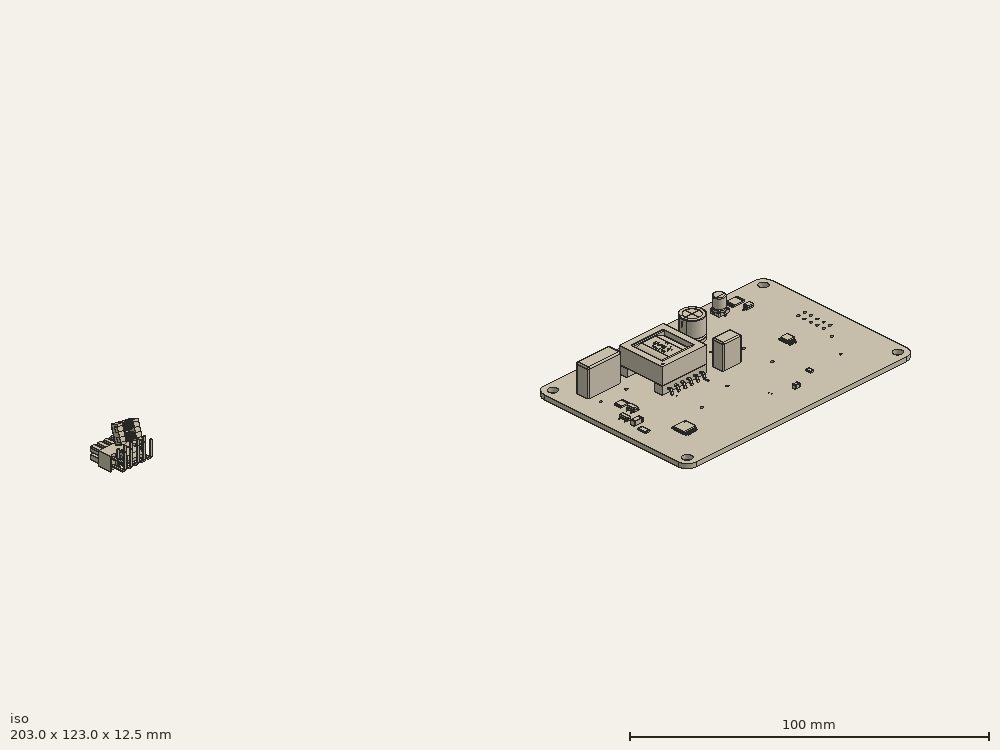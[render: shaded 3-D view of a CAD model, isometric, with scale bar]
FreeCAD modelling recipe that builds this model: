
FCSTD DOCUMENT  (FreeCAD 0.21R33694 (Git))
Label: nixiePSU
License: All rights reserved
LicenseURL: http://en.wikipedia.org/wiki/All_rights_reserved
objects: Part::Feature×79, App::Link×66, App::Part×19, PartDesign::CoordinateSystem×1, Sketcher::SketchObject×1
note: 81 computed .brp shape members not serialized (recipe doc carries the construction recipe); baked Part::Feature solids carry a one-line shape summary decoded from their .brp

FEATURE [PartDesign::CoordinateSystem] Local_CS_fa9e
  AttacherType = Attacher::AttachEngine3D
  MapMode = 2
  Support = -> [X_Axis001]
FEATURE [Part::Feature] Pcb_fa9e
  shape: bbox 90 x 60 x 1.6 mm, 44 faces (baked)
FEATURE [Sketcher::SketchObject] PCB_Sketch_fa9e
  FullyConstrained = false
  sketch-geometry (8):
    g0: LineSegment StartX=196.5 StartY=-58 StartZ=0 EndX=196.5 EndY=-111 EndZ=0
    g1: LineSegment StartX=110 StartY=-114.5 StartZ=0 EndX=193 EndY=-114.5 EndZ=0
    g2: LineSegment StartX=106.5 StartY=-58 StartZ=0 EndX=106.5 EndY=-111 EndZ=0
    g3: LineSegment StartX=110 StartY=-54.5 StartZ=0 EndX=193 EndY=-54.5 EndZ=0
    g4: ArcOfCircle CenterX=193 CenterY=-111 CenterZ=0 NormalX=0 NormalY=0 NormalZ=-1 AngleXU=3.14159 Radius=3.5 StartAngle=0 EndAngle=1.5708
    g5: ArcOfCircle CenterX=110 CenterY=-58 CenterZ=0 NormalX=0 NormalY=0 NormalZ=-1 AngleXU=-2.59331e-07 Radius=3.5 StartAngle=0 EndAngle=1.5708
    g6: ArcOfCircle CenterX=110 CenterY=-111 CenterZ=0 NormalX=0 NormalY=0 NormalZ=-1 AngleXU=-1.5708 Radius=3.5 StartAngle=0 EndAngle=1.5708
    g7: ArcOfCircle CenterX=193 CenterY=-58 CenterZ=0 NormalX=0 NormalY=0 NormalZ=-1 AngleXU=1.5708 Radius=3.5 StartAngle=0 EndAngle=1.5708
  constraints (8):
    c: Coincident(g2,g6)
    c: Coincident(g2,g5)
    c: Coincident(g1,g6)
    c: Coincident(g3,g5)
    c: Coincident(g1,g4)
    c: Coincident(g3,g7)
    c: Coincident(g0,g4)
    c: Coincident(g0,g7)
FEATURE [Part::Feature] Shape  label="U4_SOT_23_186704fecbdd"
  Placement = pos=(112.776,-83.566,0) rot=(0,0,1;0rad)
  shape: bbox 2.5 x 3 x 1.2 mm, 76 faces (baked)
FEATURE [Part::Feature] Shape001  label="C3_CP_Radial_D80mm_P350mm_9775f933acc7"
  Placement = pos=(159.653,-65,0) rot=(0,0,1;3.14159rad)
  shape: bbox 9.886 x 10.23 x 10 mm, 54 faces (baked)
FEATURE [Part::Feature] Shape002  label="C4_C_Rect_L72mm_W45mm_P500mm_FKS2_FKP2_MKS2_MKP2_e25bc456f7c6"
  Placement = pos=(157,-82,0) rot=(0,0,1;3.14159rad)
  shape: bbox 7.2 x 4.5 x 10.9 mm, 22 faces (baked)
FEATURE [Part::Feature] Shape003  label="R31_R_1206_3216Metric_a90f8c455a29"
  Placement = pos=(111.887,-91.948,0) rot=(0,0,-1;1.5708rad)
  shape: bbox 1.6 x 3.2 x 0.55 mm, 26 faces (baked)
FEATURE [Part::Feature] Shape004  label="R5_R_0805_2012Metric_dfd971a2463e"
  Placement = pos=(168.148,-101.092,0) rot=(0,0,-1;1.5708rad)
  shape: bbox 1.2 x 2 x 0.45 mm, 26 faces (baked)
FEATURE [Part::Feature] Shape005  label="C16_C_0805_2012Metric_d7ba3aa2269e"
  Placement = pos=(159.004,-104.902,0) rot=(0,0,1;0rad)
  shape: bbox 2 x 1.25 x 1.25 mm, 28 faces (baked)
FEATURE [App::Link] R5_R_0805_2012Metric_dfd971a2463e_ln_  label="R4_R_0805_2012Metric_c1b39be73899"
  LinkPlacement = pos=(161.544,-99.06,0) rot=(0,0,-1;1.5708rad)
  LinkedObject = -> Shape004
  Placement = pos=(161.544,-99.06,0) rot=(0,0,-1;1.5708rad)
FEATURE [App::Link] C16_C_0805_2012Metric_d7ba3aa2269e_ln_  label="C15_C_0805_2012Metric_97927805f462"
  LinkPlacement = pos=(146.812,-106.68,0) rot=(0,0,-1;1.5708rad)
  LinkedObject = -> Shape005
  Placement = pos=(146.812,-106.68,0) rot=(0,0,-1;1.5708rad)
FEATURE [Part::Feature] Part__Feature  label="Body"
  Placement = pos=(0,0,0.1) rot=(0,0,1;0rad)
  shape: bbox 2.5 x 3.7 x 1.05 mm, 6 faces (baked)
FEATURE [Part::Feature] Part__Feature001  label="Pins"
  shape: bbox 1.72 x 1.12 x 0.1 mm, 6 faces (baked)
FEATURE [Part::Feature] Part__Feature002  label="Pins001"
  shape: bbox 1.72 x 1.12 x 0.1 mm, 6 faces (baked)
FEATURE [App::Part] Pins  label="Pins002"
  Group = -> [Part__Feature001,Part__Feature002]
  Origin = -> Origin008
FEATURE [App::Part] ASSEMBLY  label="D2_ASSEMBLY_d7d1b7470d45[2]"
  Group = -> [Part__Feature,Pins]
  Origin = -> Origin009
  Placement = pos=(150.622,-88.392,0) rot=(0,0,1;0rad)
FEATURE [Part::Feature] Shape006  label="C33_C_1210_3225Metric_16efd0b629b8"
  Placement = pos=(150.5,-66,0) rot=(0,0,1;0rad)
  shape: bbox 3.2 x 2.5 x 2.5 mm, 28 faces (baked)
FEATURE [App::Link] R31_R_1206_3216Metric_a90f8c455a29_ln_  label="R11_R_1206_3216Metric_15b37090c9a6"
  LinkPlacement = pos=(148.59,-95.25,0) rot=(0,0,1;0rad)
  LinkedObject = -> Shape003
  Placement = pos=(148.59,-95.25,0) rot=(0,0,1;0rad)
FEATURE [App::Link] U4_SOT_23_186704fecbdd_ln_  label="Q7_SOT_23_e5c74c3ebada"
  LinkPlacement = pos=(186.164,-101.146,0) rot=(0,0,1;3.14159rad)
  LinkedObject = -> Shape
  Placement = pos=(186.164,-101.146,0) rot=(0,0,1;3.14159rad)
FEATURE [Part::Feature] Shape007  label="D1_D_SOD_123_7d86144a998e"
  Placement = pos=(181,-64,0) rot=(0,0,1;0rad)
  shape: bbox 3.8 x 1.6 x 1.25 mm, 67 faces (baked)
FEATURE [App::Link] C16_C_0805_2012Metric_d7ba3aa2269e_ln_001  label="C26_C_0805_2012Metric_950c34d4f236"
  LinkPlacement = pos=(116.281,-91.948,0) rot=(0,0,1;3.14159rad)
  LinkedObject = -> Shape005
  Placement = pos=(116.281,-91.948,0) rot=(0,0,1;3.14159rad)
FEATURE [App::Link] C16_C_0805_2012Metric_d7ba3aa2269e_ln_002  label="C23_C_0805_2012Metric_3ff7c8c4b4a5"
  LinkPlacement = pos=(168.656,-84.328,0) rot=(0,0,1;1.5708rad)
  LinkedObject = -> Shape005
  Placement = pos=(168.656,-84.328,0) rot=(0,0,1;1.5708rad)
FEATURE [App::Link] R5_R_0805_2012Metric_dfd971a2463e_ln_001  label="R16_R_0805_2012Metric_b9141e09814c"
  LinkPlacement = pos=(176.7,-70.7,0) rot=(0,0,1;1.5708rad)
  LinkedObject = -> Shape004
  Placement = pos=(176.7,-70.7,0) rot=(0,0,1;1.5708rad)
FEATURE [App::Link] R5_R_0805_2012Metric_dfd971a2463e_ln_002  label="R9_R_0805_2012Metric_3fe8031a5931"
  LinkPlacement = pos=(149.352,-106.934,0) rot=(0,0,-1;1.5708rad)
  LinkedObject = -> Shape004
  Placement = pos=(149.352,-106.934,0) rot=(0,0,-1;1.5708rad)
FEATURE [App::Link] R5_R_0805_2012Metric_dfd971a2463e_ln_003  label="locked_R_0805_2012Metric_58458bf2dea7"
  LinkPlacement = pos=(126.492,-94.234,0) rot=(0,0,1;1.5708rad)
  LinkedObject = -> Shape004
  Placement = pos=(126.492,-94.234,0) rot=(0,0,1;1.5708rad)
FEATURE [App::Link] C16_C_0805_2012Metric_d7ba3aa2269e_ln_003  label="C5_C_0805_2012Metric_2510501b0178"
  LinkPlacement = pos=(174.564,-74.146,0) rot=(0,0,1;0rad)
  LinkedObject = -> Shape005
  Placement = pos=(174.564,-74.146,0) rot=(0,0,1;0rad)
FEATURE [App::Link] C3_CP_Radial_D80mm_P350mm_9775f933acc7_ln_  label="C2_CP_Radial_D80mm_P350mm_ff32184cb77b"
  LinkPlacement = pos=(159.653,-74,0) rot=(0,0,1;3.14159rad)
  LinkedObject = -> Shape001
  Placement = pos=(159.653,-74,0) rot=(0,0,1;3.14159rad)
FEATURE [App::Link] D2_ASSEMBLY_d7d1b7470d45_2__ln_  label="D3_ASSEMBLY_34689d29e95e[2]"
  LinkPlacement = pos=(124.079,-60.452,0) rot=(0,0,-1;1.5708rad)
  LinkedObject = -> ASSEMBLY
  Placement = pos=(124.079,-60.452,0) rot=(0,0,-1;1.5708rad)
FEATURE [Part::Feature] Shape008  label="C11_C_Rect_L130mm_W50mm_P1000mm_FKS3_FKP3_MKS4_d8e08f8b682d"
  Placement = pos=(124.888,-66,0) rot=(0,0,1;3.14159rad)
  shape: bbox 13 x 5 x 11.9 mm, 22 faces (baked)
FEATURE [App::Link] U4_SOT_23_186704fecbdd_ln_001  label="Q6_SOT_23_0ca55b761fcc"
  LinkPlacement = pos=(176.064,-95.346,0) rot=(0,0,1;0rad)
  LinkedObject = -> Shape
  Placement = pos=(176.064,-95.346,0) rot=(0,0,1;0rad)
FEATURE [App::Link] R5_R_0805_2012Metric_dfd971a2463e_ln_004  label="R29_R_0805_2012Metric_df88e0cbd699"
  LinkPlacement = pos=(162.8,-84.6,0) rot=(0,0,1;1.5708rad)
  LinkedObject = -> Shape004
  Placement = pos=(162.8,-84.6,0) rot=(0,0,1;1.5708rad)
FEATURE [App::Link] C16_C_0805_2012Metric_d7ba3aa2269e_ln_004  label="C13_C_0805_2012Metric_58bcf8d5a1e2"
  LinkPlacement = pos=(156.464,-99.06,0) rot=(0,0,1;3.14159rad)
  LinkedObject = -> Shape005
  Placement = pos=(156.464,-99.06,0) rot=(0,0,1;3.14159rad)
FEATURE [App::Link] U4_SOT_23_186704fecbdd_ln_002  label="Q2_SOT_23_72d0fa22ce26"
  LinkPlacement = pos=(186.164,-96.7,0) rot=(0,0,1;3.14159rad)
  LinkedObject = -> Shape
  Placement = pos=(186.164,-96.7,0) rot=(0,0,1;3.14159rad)
FEATURE [Part::Feature] Shape009  label="locked_C_1206_3216Metric_8b2ff830be50"
  Placement = pos=(113.411,-87.63,0) rot=(0,0,1;3.14159rad)
  shape: bbox 3.2 x 1.6 x 1.6 mm, 28 faces (baked)
FEATURE [App::Link] R5_R_0805_2012Metric_dfd971a2463e_ln_005  label="R20_R_0805_2012Metric_01561e02a093"
  LinkPlacement = pos=(175,-103.5,0) rot=(0,0,1;3.14159rad)
  LinkedObject = -> Shape004
  Placement = pos=(175,-103.5,0) rot=(0,0,1;3.14159rad)
FEATURE [App::Link] C16_C_0805_2012Metric_d7ba3aa2269e_ln_005  label="C8_C_0805_2012Metric_21d7960277fa"
  LinkPlacement = pos=(156.464,-96.52,0) rot=(0,0,1;3.14159rad)
  LinkedObject = -> Shape005
  Placement = pos=(156.464,-96.52,0) rot=(0,0,1;3.14159rad)
FEATURE [App::Link] C16_C_0805_2012Metric_d7ba3aa2269e_ln_006  label="C1_C_0805_2012Metric_4264a4215c47"
  LinkPlacement = pos=(180.5,-78.7,0) rot=(0,0,1;3.14159rad)
  LinkedObject = -> Shape005
  Placement = pos=(180.5,-78.7,0) rot=(0,0,1;3.14159rad)
FEATURE [Part::Feature] Shape010  label="U3_VSSOP_8_30x30mm_P065mm_72732366a9ef"
  Placement = pos=(175.6,-84.9,0) rot=(0,0,1;1.5708rad)
  shape: bbox 3 x 4.9 x 1.35 mm, 156 faces (baked)
FEATURE [App::Link] C16_C_0805_2012Metric_d7ba3aa2269e_ln_007  label="C17_C_0805_2012Metric_806298b30b2c"
  LinkPlacement = pos=(159.004,-107.442,0) rot=(0,0,1;0rad)
  LinkedObject = -> Shape005
  Placement = pos=(159.004,-107.442,0) rot=(0,0,1;0rad)
FEATURE [App::Link] C16_C_0805_2012Metric_d7ba3aa2269e_ln_008  label="C7_C_0805_2012Metric_1a041f39c376"
  LinkPlacement = pos=(156.464,-93.726,0) rot=(0,0,1;3.14159rad)
  LinkedObject = -> Shape005
  Placement = pos=(156.464,-93.726,0) rot=(0,0,1;3.14159rad)
FEATURE [Part::Feature] Shape011  label="C18_CP_Elec_4x57_9bce058c2ef4"
  Placement = pos=(173.464,-60.046,0) rot=(0,0,-1;1.5708rad)
  shape: bbox 5.462 x 5.738 x 5.7 mm, 41 faces (baked)
FEATURE [App::Link] D2_ASSEMBLY_d7d1b7470d45_2__ln_001  label="D5_ASSEMBLY_6155feb40ac8[2]"
  LinkPlacement = pos=(158,-58.42,0) rot=(0,0,1;1.5708rad)
  LinkedObject = -> ASSEMBLY
  Placement = pos=(158,-58.42,0) rot=(0,0,1;1.5708rad)
FEATURE [App::Link] R5_R_0805_2012Metric_dfd971a2463e_ln_006  label="R15_R_0805_2012Metric_94b8bc14d4d3"
  LinkPlacement = pos=(180.848,-95.758,0) rot=(0,0,1;3.14159rad)
  LinkedObject = -> Shape004
  Placement = pos=(180.848,-95.758,0) rot=(0,0,1;3.14159rad)
FEATURE [Part::Feature] Part__Feature003  label="IPS1-105-01-D-RA_pin"
  Placement = pos=(0,-1.7272,0) rot=(0,0,1;0rad)
  shape: bbox 10.95 x 5.029 x 6.49 mm, 102 faces (baked)
FEATURE [Part::Feature] Part__Feature004  label="IPS1-105-01-L-D-RAt"
  shape: bbox 13.08 x 8.509 x 4.953 mm, 206 faces (baked)
FEATURE [App::Part] IPS1_105_01_L_D_RA  label="J1_IPS1-105-01-L-D-RA_0b1fbbf1511e"
  Group = -> [Part__Feature003,Part__Feature004]
  Origin = -> Origin010
  Placement = pos=(191.75,-82,2.5) rot=(0.707107,0.707107,0;3.14159rad)
FEATURE [App::Link] C33_C_1210_3225Metric_16efd0b629b8_ln_  label="C34_C_1210_3225Metric_06e0e1ea6feb"
  LinkPlacement = pos=(152,-60,0) rot=(0,0,-1;1.5708rad)
  LinkedObject = -> Shape006
  Placement = pos=(152,-60,0) rot=(0,0,-1;1.5708rad)
FEATURE [App::Link] C16_C_0805_2012Metric_d7ba3aa2269e_ln_009  label="C14_C_0805_2012Metric_2a316fd28da0"
  LinkPlacement = pos=(148.082,-99.822,0) rot=(0,0,1;1.5708rad)
  LinkedObject = -> Shape005
  Placement = pos=(148.082,-99.822,0) rot=(0,0,1;1.5708rad)
FEATURE [App::Link] R5_R_0805_2012Metric_dfd971a2463e_ln_007  label="R26_R_0805_2012Metric_1e05269a4dbf"
  LinkPlacement = pos=(171.9,-89,0) rot=(0,0,1;1.5708rad)
  LinkedObject = -> Shape004
  Placement = pos=(171.9,-89,0) rot=(0,0,1;1.5708rad)
FEATURE [App::Link] R31_R_1206_3216Metric_a90f8c455a29_ln_001  label="R1_R_1206_3216Metric_d501710e6ae1"
  LinkPlacement = pos=(155.448,-90.932,0) rot=(0,0,1;3.14159rad)
  LinkedObject = -> Shape003
  Placement = pos=(155.448,-90.932,0) rot=(0,0,1;3.14159rad)
FEATURE [App::Link] R5_R_0805_2012Metric_dfd971a2463e_ln_008  label="R28_R_0805_2012Metric_c060e1113165"
  LinkPlacement = pos=(168.148,-78.232,0) rot=(0,0,1;1.5708rad)
  LinkedObject = -> Shape004
  Placement = pos=(168.148,-78.232,0) rot=(0,0,1;1.5708rad)
FEATURE [App::Link] C16_C_0805_2012Metric_d7ba3aa2269e_ln_010  label="C20_C_0805_2012Metric_222437fea149"
  LinkPlacement = pos=(168.148,-94.234,0) rot=(0,0,1;3.14159rad)
  LinkedObject = -> Shape005
  Placement = pos=(168.148,-94.234,0) rot=(0,0,1;3.14159rad)
FEATURE [App::Link] R5_R_0805_2012Metric_dfd971a2463e_ln_009  label="R24_R_0805_2012Metric_a4021a96433f"
  LinkPlacement = pos=(165.084,-62.992,0) rot=(0,0,1;3.14159rad)
  LinkedObject = -> Shape004
  Placement = pos=(165.084,-62.992,0) rot=(0,0,1;3.14159rad)
FEATURE [App::Link] C16_C_0805_2012Metric_d7ba3aa2269e_ln_011  label="C22_C_0805_2012Metric_0515b9b2e578"
  LinkPlacement = pos=(175.3,-78.8,0) rot=(0,0,1;0rad)
  LinkedObject = -> Shape005
  Placement = pos=(175.3,-78.8,0) rot=(0,0,1;0rad)
FEATURE [App::Link] R5_R_0805_2012Metric_dfd971a2463e_ln_010  label="R18_R_0805_2012Metric_b0f93427f26b"
  LinkPlacement = pos=(168.64,-58.166,0) rot=(0,0,1;3.14159rad)
  LinkedObject = -> Shape004
  Placement = pos=(168.64,-58.166,0) rot=(0,0,1;3.14159rad)
FEATURE [App::Link] R5_R_0805_2012Metric_dfd971a2463e_ln_011  label="R8_R_0805_2012Metric_38d0a5a3134c"
  LinkPlacement = pos=(170.942,-100.076,0) rot=(0,0,-1;1.5708rad)
  LinkedObject = -> Shape004
  Placement = pos=(170.942,-100.076,0) rot=(0,0,-1;1.5708rad)
FEATURE [App::Link] R5_R_0805_2012Metric_dfd971a2463e_ln_012  label="R10_R_0805_2012Metric_cee45a7546ea"
  LinkPlacement = pos=(143,-105.5,0) rot=(0,0,1;3.14159rad)
  LinkedObject = -> Shape004
  Placement = pos=(143,-105.5,0) rot=(0,0,1;3.14159rad)
FEATURE [App::Link] U4_SOT_23_186704fecbdd_ln_003  label="Q5_SOT_23_91ededf4ea50"
  LinkPlacement = pos=(122.667,-83.693,0) rot=(0,0,1;0rad)
  LinkedObject = -> Shape
  Placement = pos=(122.667,-83.693,0) rot=(0,0,1;0rad)
FEATURE [Part::Feature] Part__Feature005  label="SOLID"
  shape: bbox 0.4 x 0.1 x 0.45 mm, 9 faces (baked)
FEATURE [Part::Feature] Part__Feature006  label="SOLID001"
  shape: bbox 0.4 x 0.1 x 0.25 mm, 6 faces (baked)
FEATURE [Part::Feature] Part__Feature007  label="SOLID002"
  shape: bbox 0.4 x 0.1 x 0.25 mm, 6 faces (baked)
FEATURE [Part::Feature] Part__Feature008  label="SOLID003"
  shape: bbox 0.4 x 0.1 x 0.45 mm, 9 faces (baked)
FEATURE [Part::Feature] Part__Feature009  label="SOLID004"
  shape: bbox 0.3 x 0.1 x 2 mm, 6 faces (baked)
FEATURE [Part::Feature] Part__Feature010  label="SOLID005"
  shape: bbox 0.3 x 0.1 x 2 mm, 6 faces (baked)
FEATURE [Part::Feature] Part__Feature011  label="SOLID006"
  shape: bbox 0.4 x 0.1 x 0.45 mm, 9 faces (baked)
FEATURE [Part::Feature] Part__Feature012  label="SOLID007"
  shape: bbox 0.4 x 0.1 x 0.25 mm, 6 faces (baked)
FEATURE [Part::Feature] Part__Feature013  label="SOLID008"
  shape: bbox 0.4 x 0.1 x 0.25 mm, 6 faces (baked)
FEATURE [Part::Feature] Part__Feature014  label="SOLID009"
  shape: bbox 0.4 x 0.1 x 0.45 mm, 9 faces (baked)
FEATURE [App::Part] FRAME
  Group = -> [Part__Feature005,Part__Feature006,Part__Feature007,Part__Feature008,Part__Feature009,Part__Feature010,Part__Feature011,Part__Feature012,Part__Feature013,Part__Feature014]
  Origin = -> Origin011
  Placement = pos=(0,0,0) rot=(1,0,0;1.5708rad)
FEATURE [Part::Feature] Part__Feature015  label="MOLD"
  Placement = pos=(0,0,0.025) rot=(1,0,0;1.5708rad)
  shape: bbox 2 x 2 x 0.975 mm, 58 faces (baked)
FEATURE [App::Part] RPW0010A_ASM  label="U2_RPW0010A_ASM_12f05aba0fd9"
  Group = -> [FRAME,Part__Feature015]
  Origin = -> Origin012
  Placement = pos=(170.914,-69.646,0) rot=(0,0,1;3.14159rad)
FEATURE [App::Link] C33_C_1210_3225Metric_16efd0b629b8_ln_001  label="C31_C_1210_3225Metric_6e1f27100fa0"
  LinkPlacement = pos=(150.5,-73,0) rot=(0,0,1;0rad)
  LinkedObject = -> Shape006
  Placement = pos=(150.5,-73,0) rot=(0,0,1;0rad)
FEATURE [App::Link] R5_R_0805_2012Metric_dfd971a2463e_ln_013  label="R34_R_0805_2012Metric_614447377eb4"
  LinkPlacement = pos=(126.2,-105.6,0) rot=(0,0,-1;1.5708rad)
  LinkedObject = -> Shape004
  Placement = pos=(126.2,-105.6,0) rot=(0,0,-1;1.5708rad)
FEATURE [Part::Feature] Shape012  label="R2_R_1210_3225Metric_fbc89a17cad0"
  Placement = pos=(117.856,-77.216,0) rot=(0,0,1;3.14159rad)
  shape: bbox 3.2 x 2.5 x 0.55 mm, 26 faces (baked)
FEATURE [App::Link] D1_D_SOD_123_7d86144a998e_ln_  label="D6_D_SOD_123_ef05caf814b4"
  LinkPlacement = pos=(165,-72.39,0) rot=(0,0,1;3.14159rad)
  LinkedObject = -> Shape007
  Placement = pos=(165,-72.39,0) rot=(0,0,1;3.14159rad)
FEATURE [App::Link] C33_C_1210_3225Metric_16efd0b629b8_ln_002  label="C9_C_1210_3225Metric_66f0a5e9d645"
  LinkPlacement = pos=(155.448,-87.63,0) rot=(0,0,1;3.14159rad)
  LinkedObject = -> Shape006
  Placement = pos=(155.448,-87.63,0) rot=(0,0,1;3.14159rad)
FEATURE [App::Link] R5_R_0805_2012Metric_dfd971a2463e_ln_014  label="R19_R_0805_2012Metric_974e4cfe6736"
  LinkPlacement = pos=(174.482,-66.04,0) rot=(0,0,1;3.14159rad)
  LinkedObject = -> Shape004
  Placement = pos=(174.482,-66.04,0) rot=(0,0,1;3.14159rad)
FEATURE [Part::Feature] Shape013  label="U6_TSSOP_14_44x5mm_P065mm_3d0a8b7a1a53"
  Placement = pos=(120.5,-99.3,0) rot=(0,0,-1;1.5708rad)
  shape: bbox 5 x 6.4 x 1 mm, 246 faces (baked)
FEATURE [App::Link] C33_C_1210_3225Metric_16efd0b629b8_ln_003  label="C30_C_1210_3225Metric_3da81cda1102"
  LinkPlacement = pos=(150.5,-69.5,0) rot=(0,0,1;0rad)
  LinkedObject = -> Shape006
  Placement = pos=(150.5,-69.5,0) rot=(0,0,1;0rad)
FEATURE [App::Link] R5_R_0805_2012Metric_dfd971a2463e_ln_015  label="R17_R_0805_2012Metric_d3106368d4ac"
  LinkPlacement = pos=(179.6,-73.8,0) rot=(0,0,1;1.5708rad)
  LinkedObject = -> Shape004
  Placement = pos=(179.6,-73.8,0) rot=(0,0,1;1.5708rad)
FEATURE [App::Link] C16_C_0805_2012Metric_d7ba3aa2269e_ln_012  label="C28_C_0805_2012Metric_21ff8b1a5ae6"
  LinkPlacement = pos=(123.8,-105.6,0) rot=(0,0,1;1.5708rad)
  LinkedObject = -> Shape005
  Placement = pos=(123.8,-105.6,0) rot=(0,0,1;1.5708rad)
FEATURE [App::Link] C18_CP_Elec_4x57_9bce058c2ef4_ln_  label="C29_CP_Elec_4x57_21e76817bfe8"
  LinkPlacement = pos=(114.2,-99.1,0) rot=(0,0,-1;1.5708rad)
  LinkedObject = -> Shape011
  Placement = pos=(114.2,-99.1,0) rot=(0,0,-1;1.5708rad)
FEATURE [Part::Feature] Part__Feature016  label="932d09b3-9c39-11ed-93f0-dde97e994e83_part"
  shape: bbox 6.22 x 6.5 x 2.3 mm, 13 faces (baked)
FEATURE [App::Part] _32d09b3_9c39_11ed_93f0_dde97e994e83  label="932d09b3-9c39-11ed-93f0-dde97e994e83"
  Group = -> [Part__Feature016]
  Origin = -> Origin013
FEATURE [Part::Feature] Part__Feature017  label="932d09b4-9c39-11ed-93f0-dde97e994e83_part"
  shape: bbox 5.24 x 5.4 x 0.5 mm, 16 faces (baked)
FEATURE [App::Part] _32d09b4_9c39_11ed_93f0_dde97e994e83  label="932d09b4-9c39-11ed-93f0-dde97e994e83"
  Group = -> [Part__Feature017]
  Origin = -> Origin014
FEATURE [Part::Feature] Part__Feature018  label="932d09b5-9c39-11ed-93f0-dde97e994e83_part"
  shape: bbox 3.552 x 0.99 x 1.44 mm, 22 faces (baked)
FEATURE [Part::Feature] Part__Feature019  label="932d09b5-9c39-11ed-93f0-dde97e994e83_part001"
  shape: bbox 1.672 x 0.99 x 0.5 mm, 10 faces (baked)
FEATURE [Part::Feature] Part__Feature020  label="932d09b5-9c39-11ed-93f0-dde97e994e83_part002"
  shape: bbox 3.552 x 0.99 x 1.44 mm, 22 faces (baked)
FEATURE [App::Part] _32d09b5_9c39_11ed_93f0_dde97e994e83_part  label="932d09b5-9c39-11ed-93f0-dde97e994e83_part003"
  Group = -> [Part__Feature018,Part__Feature019,Part__Feature020]
  Origin = -> Origin015
FEATURE [App::Part] _32d09b5_9c39_11ed_93f0_dde97e994e83  label="932d09b5-9c39-11ed-93f0-dde97e994e83"
  Group = -> [_32d09b5_9c39_11ed_93f0_dde97e994e83_part]
  Origin = -> Origin016
FEATURE [App::Part] _32d09b2_9c39_11ed_93f0_dde97e994e83  label="932d09b2-9c39-11ed-93f0-dde97e994e83"
  Group = -> [_32d09b3_9c39_11ed_93f0_dde97e994e83,_32d09b4_9c39_11ed_93f0_dde97e994e83,_32d09b5_9c39_11ed_93f0_dde97e994e83]
  Origin = -> Origin017
FEATURE [App::Part] CQ_assembly  label="Q1_CQ assembly_247b2b5b2e2c"
  Group = -> [_32d09b2_9c39_11ed_93f0_dde97e994e83]
  Origin = -> Origin018
  Placement = pos=(139.192,-92.378,0) rot=(0,0,1;1.5708rad)
FEATURE [App::Link] R5_R_0805_2012Metric_dfd971a2463e_ln_016  label="R12_R_0805_2012Metric_e9800049af57"
  LinkPlacement = pos=(159.004,-102.616,0) rot=(0,0,1;0rad)
  LinkedObject = -> Shape004
  Placement = pos=(159.004,-102.616,0) rot=(0,0,1;0rad)
FEATURE [App::Link] R5_R_0805_2012Metric_dfd971a2463e_ln_017  label="R27_R_0805_2012Metric_9d2c688d584c"
  LinkPlacement = pos=(175.8,-91,0) rot=(0,0,1;3.14159rad)
  LinkedObject = -> Shape004
  Placement = pos=(175.8,-91,0) rot=(0,0,1;3.14159rad)
FEATURE [App::Link] C16_C_0805_2012Metric_d7ba3aa2269e_ln_013  label="C21_C_0805_2012Metric_81d71a5b1e96"
  LinkPlacement = pos=(165.664,-66.746,0) rot=(0,0,1;3.14159rad)
  LinkedObject = -> Shape005
  Placement = pos=(165.664,-66.746,0) rot=(0,0,1;3.14159rad)
FEATURE [App::Link] D1_D_SOD_123_7d86144a998e_ln_001  label="D4_D_SOD_123_98dec9aebbc3"
  LinkPlacement = pos=(175.006,-100.076,0) rot=(0,0,1;3.14159rad)
  LinkedObject = -> Shape007
  Placement = pos=(175.006,-100.076,0) rot=(0,0,1;3.14159rad)
FEATURE [App::Link] R5_R_0805_2012Metric_dfd971a2463e_ln_018  label="R6_R_0805_2012Metric_b739daf2c9fc"
  LinkPlacement = pos=(126.365,-90.932,0) rot=(0,0,1;0rad)
  LinkedObject = -> Shape004
  Placement = pos=(126.365,-90.932,0) rot=(0,0,1;0rad)
FEATURE [App::Link] R5_R_0805_2012Metric_dfd971a2463e_ln_019  label="R7_R_0805_2012Metric_bdb415347411"
  LinkPlacement = pos=(142.9,-101.9,0) rot=(0,0,1;3.14159rad)
  LinkedObject = -> Shape004
  Placement = pos=(142.9,-101.9,0) rot=(0,0,1;3.14159rad)
FEATURE [Part::Feature] Shape014  label="TR1_Coilcraft-DA2033-AL_34ac942f81a4"
  Placement = pos=(138.168,-73.16,0) rot=(0.57735,0.57735,0.57735;2.0944rad)
  shape: bbox 17.4 x 24.13 x 9.602 mm, 540 faces (baked)
FEATURE [App::Link] C33_C_1210_3225Metric_16efd0b629b8_ln_004  label="C32_C_1210_3225Metric_3a8b2a19532b"
  LinkPlacement = pos=(150.5,-76.5,0) rot=(0,0,1;0rad)
  LinkedObject = -> Shape006
  Placement = pos=(150.5,-76.5,0) rot=(0,0,1;0rad)
FEATURE [App::Link] C16_C_0805_2012Metric_d7ba3aa2269e_ln_014  label="C27_C_0805_2012Metric_f83e7b3e5d35"
  LinkPlacement = pos=(127.1,-99.3,0) rot=(0,0,1;1.5708rad)
  LinkedObject = -> Shape005
  Placement = pos=(127.1,-99.3,0) rot=(0,0,1;1.5708rad)
FEATURE [App::Link] C16_C_0805_2012Metric_d7ba3aa2269e_ln_015  label="C24_C_0805_2012Metric_a5a4b744a6d0"
  LinkPlacement = pos=(165.5,-84.6,0) rot=(0,0,-1;1.5708rad)
  LinkedObject = -> Shape005
  Placement = pos=(165.5,-84.6,0) rot=(0,0,-1;1.5708rad)
FEATURE [App::Link] C11_C_Rect_L130mm_W50mm_P1000mm_FKS3_FKP3_MKS4_d8e08f8b682d_ln_  label="C10_C_Rect_L130mm_W50mm_P1000mm_FKS3_FKP3_MKS4_9deb56838e9d"
  LinkPlacement = pos=(124.888,-72.009,0) rot=(0,0,1;3.14159rad)
  LinkedObject = -> Shape008
  Placement = pos=(124.888,-72.009,0) rot=(0,0,1;3.14159rad)
FEATURE [App::Link] R5_R_0805_2012Metric_dfd971a2463e_ln_020  label="R22_R_0805_2012Metric_3f6000836c75"
  LinkPlacement = pos=(165.164,-69.646,0) rot=(0,0,1;3.14159rad)
  LinkedObject = -> Shape004
  Placement = pos=(165.164,-69.646,0) rot=(0,0,1;3.14159rad)
FEATURE [Part::Feature] Shape015  label="F1_R_1812_4532Metric_b15bc011db9b"
  Placement = pos=(180.324,-59.436,0) rot=(0,0,1;3.14159rad)
  shape: bbox 4.5 x 3.2 x 0.6 mm, 26 faces (baked)
FEATURE [App::Link] R5_R_0805_2012Metric_dfd971a2463e_ln_021  label="R32_R_0805_2012Metric_904646e41a0c"
  LinkPlacement = pos=(123.063,-79.756,0) rot=(0,0,1;1.5708rad)
  LinkedObject = -> Shape004
  Placement = pos=(123.063,-79.756,0) rot=(0,0,1;1.5708rad)
FEATURE [Part::Feature] Part__Feature021  label="BODY-SON"
  Placement = pos=(0,0,0.05) rot=(1,0,0;1.5708rad)
  shape: bbox 2 x 3 x 0.75 mm, 77 faces (baked)
FEATURE [Part::Feature] Part__Feature022  label="SOLID010"
  shape: bbox 1.1 x 0.2 x 3 mm, 28 faces (baked)
FEATURE [Part::Feature] Part__Feature023  label="SOLID011"
  shape: bbox 0.3 x 0.2 x 0.25 mm, 6 faces (baked)
FEATURE [Part::Feature] Part__Feature024  label="SOLID012"
  shape: bbox 0.3 x 0.2 x 0.25 mm, 6 faces (baked)
FEATURE [Part::Feature] Part__Feature025  label="SOLID013"
  shape: bbox 0.3 x 0.2 x 0.25 mm, 6 faces (baked)
FEATURE [Part::Feature] Part__Feature026  label="SOLID014"
  shape: bbox 0.3 x 0.2 x 0.25 mm, 6 faces (baked)
FEATURE [Part::Feature] Part__Feature027  label="SOLID015"
  shape: bbox 0.3 x 0.2 x 0.25 mm, 6 faces (baked)
FEATURE [Part::Feature] Part__Feature028  label="SOLID016"
  shape: bbox 0.3 x 0.2 x 0.25 mm, 6 faces (baked)
FEATURE [Part::Feature] Part__Feature029  label="SOLID017"
  shape: bbox 0.3 x 0.2 x 0.25 mm, 6 faces (baked)
FEATURE [Part::Feature] Part__Feature030  label="SOLID018"
  shape: bbox 0.3 x 0.2 x 0.25 mm, 6 faces (baked)
FEATURE [Part::Feature] Part__Feature031  label="SOLID019"
  shape: bbox 0.3 x 0.2 x 0.25 mm, 6 faces (baked)
FEATURE [Part::Feature] Part__Feature032  label="SOLID020"
  shape: bbox 0.3 x 0.2 x 0.25 mm, 6 faces (baked)
FEATURE [Part::Feature] Part__Feature033  label="SOLID021"
  shape: bbox 0.3 x 0.2 x 0.25 mm, 6 faces (baked)
FEATURE [Part::Feature] Part__Feature034  label="SOLID022"
  shape: bbox 0.3 x 0.2 x 0.25 mm, 6 faces (baked)
FEATURE [App::Part] FRAME_DSS0012B  label="FRAME-DSS0012B"
  Group = -> [Part__Feature022,Part__Feature023,Part__Feature024,Part__Feature025,Part__Feature026,Part__Feature027,Part__Feature028,Part__Feature029,Part__Feature030,Part__Feature031,Part__Feature032,Part__Feature033,Part__Feature034]
  Origin = -> Origin019
  Placement = pos=(0,0,0) rot=(1,0,0;1.5708rad)
FEATURE [App::Part] DSS0012B_ASM  label="U1_DSS0012B_ASM_e30d91bf15c6"
  Group = -> [Part__Feature021,FRAME_DSS0012B]
  Origin = -> Origin020
  Placement = pos=(151.638,-102.616,0) rot=(0,0,1;0rad)
FEATURE [App::Link] C16_C_0805_2012Metric_d7ba3aa2269e_ln_016  label="C6_C_0805_2012Metric_43810d3bc49b"
  LinkPlacement = pos=(146.05,-58.166,0) rot=(0,0,1;0rad)
  LinkedObject = -> Shape005
  Placement = pos=(146.05,-58.166,0) rot=(0,0,1;0rad)
FEATURE [App::Link] C16_C_0805_2012Metric_d7ba3aa2269e_ln_017  label="C12_C_0805_2012Metric_3f68a923801c"
  LinkPlacement = pos=(127.508,-88.265,0) rot=(0,0,1;0rad)
  LinkedObject = -> Shape005
  Placement = pos=(127.508,-88.265,0) rot=(0,0,1;0rad)
FEATURE [App::Link] R5_R_0805_2012Metric_dfd971a2463e_ln_022  label="R23_R_0805_2012Metric_c62f447cce12"
  LinkPlacement = pos=(184.4,-81.9,0) rot=(0,0,1;0rad)
  LinkedObject = -> Shape004
  Placement = pos=(184.4,-81.9,0) rot=(0,0,1;0rad)
FEATURE [App::Link] R5_R_0805_2012Metric_dfd971a2463e_ln_023  label="R25_R_0805_2012Metric_7e0de06674d9"
  LinkPlacement = pos=(171.4,-77.9,0) rot=(0,0,-1;1.5708rad)
  LinkedObject = -> Shape004
  Placement = pos=(171.4,-77.9,0) rot=(0,0,-1;1.5708rad)
FEATURE [App::Link] R5_R_0805_2012Metric_dfd971a2463e_ln_024  label="R14_R_0805_2012Metric_ddfc7b182f70"
  LinkPlacement = pos=(171.704,-95.25,0) rot=(0,0,1;1.5708rad)
  LinkedObject = -> Shape004
  Placement = pos=(171.704,-95.25,0) rot=(0,0,1;1.5708rad)
FEATURE [App::Link] R5_R_0805_2012Metric_dfd971a2463e_ln_025  label="R21_R_0805_2012Metric_786ed88a5e91"
  LinkPlacement = pos=(165.084,-60.706,0) rot=(0,0,1;0rad)
  LinkedObject = -> Shape004
  Placement = pos=(165.084,-60.706,0) rot=(0,0,1;0rad)
FEATURE [App::Link] R5_R_0805_2012Metric_dfd971a2463e_ln_026  label="R13_R_0805_2012Metric_2cbbe7c97282"
  LinkPlacement = pos=(154.178,-107.442,0) rot=(0,0,1;3.14159rad)
  LinkedObject = -> Shape004
  Placement = pos=(154.178,-107.442,0) rot=(0,0,1;3.14159rad)
FEATURE [App::Link] C16_C_0805_2012Metric_d7ba3aa2269e_ln_018  label="C19_C_0805_2012Metric_72c93020a286"
  LinkPlacement = pos=(170.064,-64.346,0) rot=(0,0,1;0rad)
  LinkedObject = -> Shape005
  Placement = pos=(170.064,-64.346,0) rot=(0,0,1;0rad)
FEATURE [App::Link] R5_R_0805_2012Metric_dfd971a2463e_ln_027  label="R30_R_0805_2012Metric_478416ca47c6"
  LinkPlacement = pos=(120.65,-91.948,0) rot=(0,0,1;3.14159rad)
  LinkedObject = -> Shape004
  Placement = pos=(120.65,-91.948,0) rot=(0,0,1;3.14159rad)
FEATURE [App::Link] R5_R_0805_2012Metric_dfd971a2463e_ln_028  label="R3_R_0805_2012Metric_9904cfb949a0"
  LinkPlacement = pos=(120.777,-88.011,0) rot=(0,0,-1;1.5708rad)
  LinkedObject = -> Shape004
  Placement = pos=(120.777,-88.011,0) rot=(0,0,-1;1.5708rad)
FEATURE [Part::Feature] Shape016  label="U5_SOT_23_5_94c5e7020abf"
  Placement = pos=(117.729,-81.534,0) rot=(0,0,1;3.14159rad)
  shape: bbox 2.8 x 2.9 x 1.55 mm, 109 faces (baked)
FEATURE [Part::Feature] Part__Feature035  label="PA4339I"
  Placement = pos=(2.67343,4.10604,5.15856) rot=(0.993886,-0.103722,-0.037859;2.71223rad)
  shape: bbox 7.542 x 4.316 x 5.972 mm, 20 faces (baked)
FEATURE [Part::Feature] Part__Feature036  label="PA4339ii"
  Placement = pos=(2.07594,1.17335,6.54866) rot=(-0.892132,0.154905,-0.424387;0.482245rad)
  shape: bbox 1.458 x 3.182 x 3.06 mm, 16 faces (baked)
FEATURE [Part::Feature] Part__Feature037  label="PA4339ii001"
  Placement = pos=(2.07594,1.17335,6.54866) rot=(-0.892132,0.154905,-0.424387;0.482245rad)
  shape: bbox 2.22 x 2.414 x 2.085 mm, 6 faces (baked)
FEATURE [Part::Feature] Part__Feature038  label="PA4339ii002"
  Placement = pos=(2.07594,1.17335,6.54866) rot=(-0.892132,0.154905,-0.424387;0.482245rad)
  shape: bbox 1.458 x 3.182 x 3.06 mm, 16 faces (baked)
FEATURE [Part::Feature] Part__Feature039  label="PA4339ii003"
  Placement = pos=(2.07594,1.17335,6.54866) rot=(-0.892132,0.154905,-0.424387;0.482245rad)
  shape: bbox 1.458 x 3.182 x 3.06 mm, 16 faces (baked)
FEATURE [Part::Feature] Part__Feature040  label="PA4339ii004"
  Placement = pos=(2.07594,1.17335,6.54866) rot=(-0.892132,0.154905,-0.424387;0.482245rad)
  shape: bbox 1.458 x 3.182 x 3.06 mm, 16 faces (baked)
FEATURE [Part::Feature] Part__Feature041  label="PA4339ii005"
  Placement = pos=(2.07594,1.17335,6.54866) rot=(-0.892132,0.154905,-0.424387;0.482245rad)
  shape: bbox 8.067 x 6.648 x 6.94 mm, 52 faces (baked)
FEATURE [Part::Feature] Part__Feature042  label="PA4339ii006"
  Placement = pos=(2.07594,1.17335,6.54866) rot=(-0.892132,0.154905,-0.424387;0.482245rad)
  shape: bbox 1.458 x 3.182 x 3.06 mm, 16 faces (baked)
FEATURE [Part::Feature] Part__Feature043  label="PA4339ii007"
  Placement = pos=(2.07594,1.17335,6.54866) rot=(-0.892132,0.154905,-0.424387;0.482245rad)
  shape: bbox 1.458 x 3.182 x 3.06 mm, 16 faces (baked)
FEATURE [Part::Feature] Part__Feature044  label="PA4339ii008"
  Placement = pos=(2.07594,1.17335,6.54866) rot=(-0.892132,0.154905,-0.424387;0.482245rad)
  shape: bbox 1.458 x 3.182 x 3.06 mm, 16 faces (baked)
FEATURE [Part::Feature] Part__Feature045  label="PA4339ii009"
  Placement = pos=(2.07594,1.17335,6.54866) rot=(-0.892132,0.154905,-0.424387;0.482245rad)
  shape: bbox 2.22 x 2.414 x 2.085 mm, 6 faces (baked)
FEATURE [Part::Feature] Part__Feature046  label="PA4339ii010"
  Placement = pos=(2.07594,1.17335,6.54866) rot=(-0.892132,0.154905,-0.424387;0.482245rad)
  shape: bbox 2.22 x 2.414 x 2.085 mm, 6 faces (baked)
FEATURE [Part::Feature] Part__Feature047  label="PA4339ii011"
  Placement = pos=(2.07594,1.17335,6.54866) rot=(-0.892132,0.154905,-0.424387;0.482245rad)
  shape: bbox 1.458 x 3.182 x 3.06 mm, 16 faces (baked)
FEATURE [Part::Feature] Part__Feature048  label="PA4339ii012"
  Placement = pos=(2.07594,1.17335,6.54866) rot=(-0.892132,0.154905,-0.424387;0.482245rad)
  shape: bbox 1.458 x 3.182 x 3.06 mm, 16 faces (baked)
FEATURE [Part::Feature] Part__Feature049  label="PA4339ii013"
  Placement = pos=(2.07594,1.17335,6.54866) rot=(-0.892132,0.154905,-0.424387;0.482245rad)
  shape: bbox 1.458 x 3.182 x 3.06 mm, 16 faces (baked)
FEATURE [Part::Feature] Part__Feature050  label="PA4339ii014"
  Placement = pos=(2.07594,1.17335,6.54866) rot=(-0.892132,0.154905,-0.424387;0.482245rad)
  shape: bbox 2.22 x 2.414 x 2.085 mm, 6 faces (baked)
FEATURE [Part::Feature] Part__Feature051  label="PA4339ii015"
  Placement = pos=(2.07594,1.17335,6.54866) rot=(-0.892132,0.154905,-0.424387;0.482245rad)
  shape: bbox 1.458 x 3.182 x 3.06 mm, 16 faces (baked)
FEATURE [Part::Feature] Part__Feature052  label="PA4339ii016"
  Placement = pos=(2.07594,1.17335,6.54866) rot=(-0.892132,0.154905,-0.424387;0.482245rad)
  shape: bbox 1.458 x 3.182 x 3.06 mm, 16 faces (baked)
FEATURE [Part::Feature] Part__Feature053  label="PA4339ii017"
  Placement = pos=(2.07594,1.17335,6.54866) rot=(-0.892132,0.154905,-0.424387;0.482245rad)
  shape: bbox 1.458 x 3.182 x 3.06 mm, 16 faces (baked)
FEATURE [Part::Feature] Part__Feature054  label="PA4339ii018"
  Placement = pos=(2.07594,1.17335,6.54866) rot=(-0.892132,0.154905,-0.424387;0.482245rad)
  shape: bbox 1.458 x 3.182 x 3.06 mm, 16 faces (baked)
FEATURE [App::Part] PA4339ii  label="PA4339ii019"
  Group = -> [Part__Feature036,Part__Feature037,Part__Feature038,Part__Feature039,Part__Feature040,Part__Feature041,Part__Feature042,Part__Feature043,Part__Feature044,Part__Feature045,Part__Feature046,Part__Feature047,Part__Feature048,Part__Feature049,Part__Feature050,Part__Feature051,Part__Feature052,Part__Feature053,Part__Feature054]
  Origin = -> Origin021
FEATURE [App::Part] PA4339_101NLT  label="L1_PA4339.101NLT_b149b3c20ede"
  Group = -> [Part__Feature035,PA4339ii]
  Origin = -> Origin022
  Placement = pos=(194.5,-68,1.5) rot=(-0.574466,0.725555,0.378891;3.97589rad)
FEATURE [App::Part] Top_fa9e
  Group = -> [Shape,Shape001,Shape002,Shape003,Shape004,Shape005,R5_R_0805_2012Metric_dfd971a2463e_ln_,C16_C_0805_2012Metric_d7ba3aa2269e_ln_,ASSEMBLY,Shape006,R31_R_1206_3216Metric_a90f8c455a29_ln_,U4_SOT_23_186704fecbdd_ln_,Shape007,C16_C_0805_2012Metric_d7ba3aa2269e_ln_001,C16_C_0805_2012Metric_d7ba3aa2269e_ln_002,R5_R_0805_2012Metric_dfd971a2463e_ln_001,R5_R_0805_2012Metric_dfd971a2463e_ln_002,+72 more]
  Origin = -> Origin003
FEATURE [App::Part] Step_Models_fa9e
  Group = -> [Top_fa9e]
  Origin = -> Origin002
FEATURE [Part::Feature] Shape018  label="topTracks_fa9e"
  Placement = pos=(0,0,0.01) rot=(0,0,1;0rad)
  shape: bbox 80.31 x 52.26 x 2e-07 mm, 83 faces, 0 solids (baked)
FEATURE [Part::Feature] zones_area001  label="topZones_fa9e"
  Placement = pos=(0,0,0.01) rot=(0,0,1;0rad)
  shape: bbox 88.85 x 58.85 x 2e-07 mm, 17 faces, 0 solids (baked)
FEATURE [Part::Feature] topPads_fa9e_  label="topPads_fa9e_cut"
  Placement = pos=(0,0,0.02) rot=(0,0,1;0rad)
  shape: bbox 85.6 x 56.85 x 2e-07 mm, 509 faces, 0 solids (baked)
FEATURE [Part::Feature] pads_area003  label="botPads_fa9e"
  Placement = pos=(0,0,-1.62) rot=(0,0,1;0rad)
  shape: bbox 85.6 x 56.85 x 2e-07 mm, 288 faces, 0 solids (baked)
FEATURE [Part::Feature] Shape020  label="botTracks_fa9e"
  Placement = pos=(0,0,-1.61) rot=(0,0,1;0rad)
  shape: bbox 81.66 x 52.14 x 2e-07 mm, 18 faces, 0 solids (baked)
FEATURE [Part::Feature] zones_area003  label="botZones_fa9e"
  Placement = pos=(0,0,-1.61) rot=(0,0,1;0rad)
  shape: bbox 88.85 x 58.85 x 2e-07 mm, 3 faces, 0 solids (baked)
FEATURE [App::Part] Board_Geoms_fa9e
  Group = -> [Pcb_fa9e,PCB_Sketch_fa9e,topPads_fa9e_,Shape018,zones_area001,pads_area003,Shape020,zones_area003]
  Origin = -> Origin
FEATURE [App::Part] Board_fa9e  label="Nixie PSU"
  Group = -> [Local_CS_fa9e,Board_Geoms_fa9e,Step_Models_fa9e]
  Origin = -> Origin001
